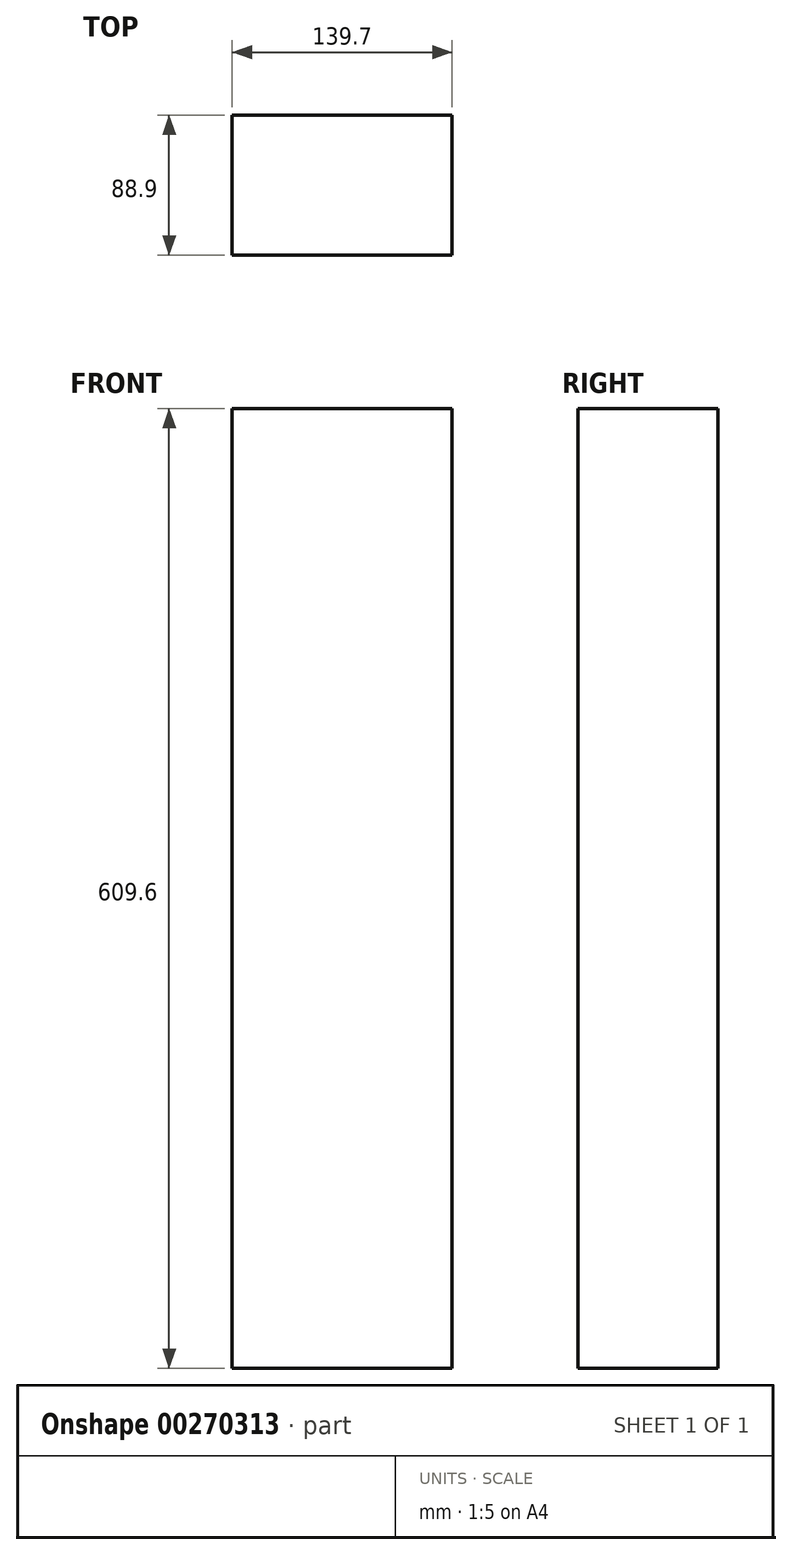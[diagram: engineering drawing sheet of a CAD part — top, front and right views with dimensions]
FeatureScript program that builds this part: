
annotation { "Feature Type Name" : "Feature", "Feature Type Description" : "" }
export const myFeature = defineFeature(function(context is Context, id is Id, definition is map)
    precondition{}
    {
        {
            var Q0;
            Q0=qCreatedBy(makeId("Top.planeOp"),FACE);
            var sketch = newSketch(context, id + "F0", { "sketchPlane" : qUnion([Q0])});
            skLineSegment(sketch, "E0.bottom", {"start": v(69.85, -44.45) * mm, "end": v(-69.85, -44.45) * mm});
            skLineSegment(sketch, "E0.top", {"start": v(69.85, 44.45) * mm, "end": v(-69.85, 44.45) * mm});
            skLineSegment(sketch, "E0.left", {"start": v(69.85, -44.45) * mm, "end": v(69.85, 44.45) * mm});
            skLineSegment(sketch, "E0.right", {"start": v(-69.85, -44.45) * mm, "end": v(-69.85, 44.45) * mm});
            skPoint(sketch, "E0.middle", {"position": v(0, 0) * mm});
            skSolve(sketch);
        }
        {
            var Q0;
            Q0=makeQuery(id+"F0.imprint","IMPRINT",FACE,{"disambiguationData":[TD([[makeQuery(id+"F0.imprint","IMPRINT",EDGE,{"derivedFrom":sQuery(id+"F0.wireOp",EDGE,"E0.bottom")}),-1.0]])]});
            extrude(context, id + "F1", {"entities" : qUnion([Q0]), "endBound" : BoundingType.SYMMETRIC, "depth" : 609.6 * mm});
        }
    });
